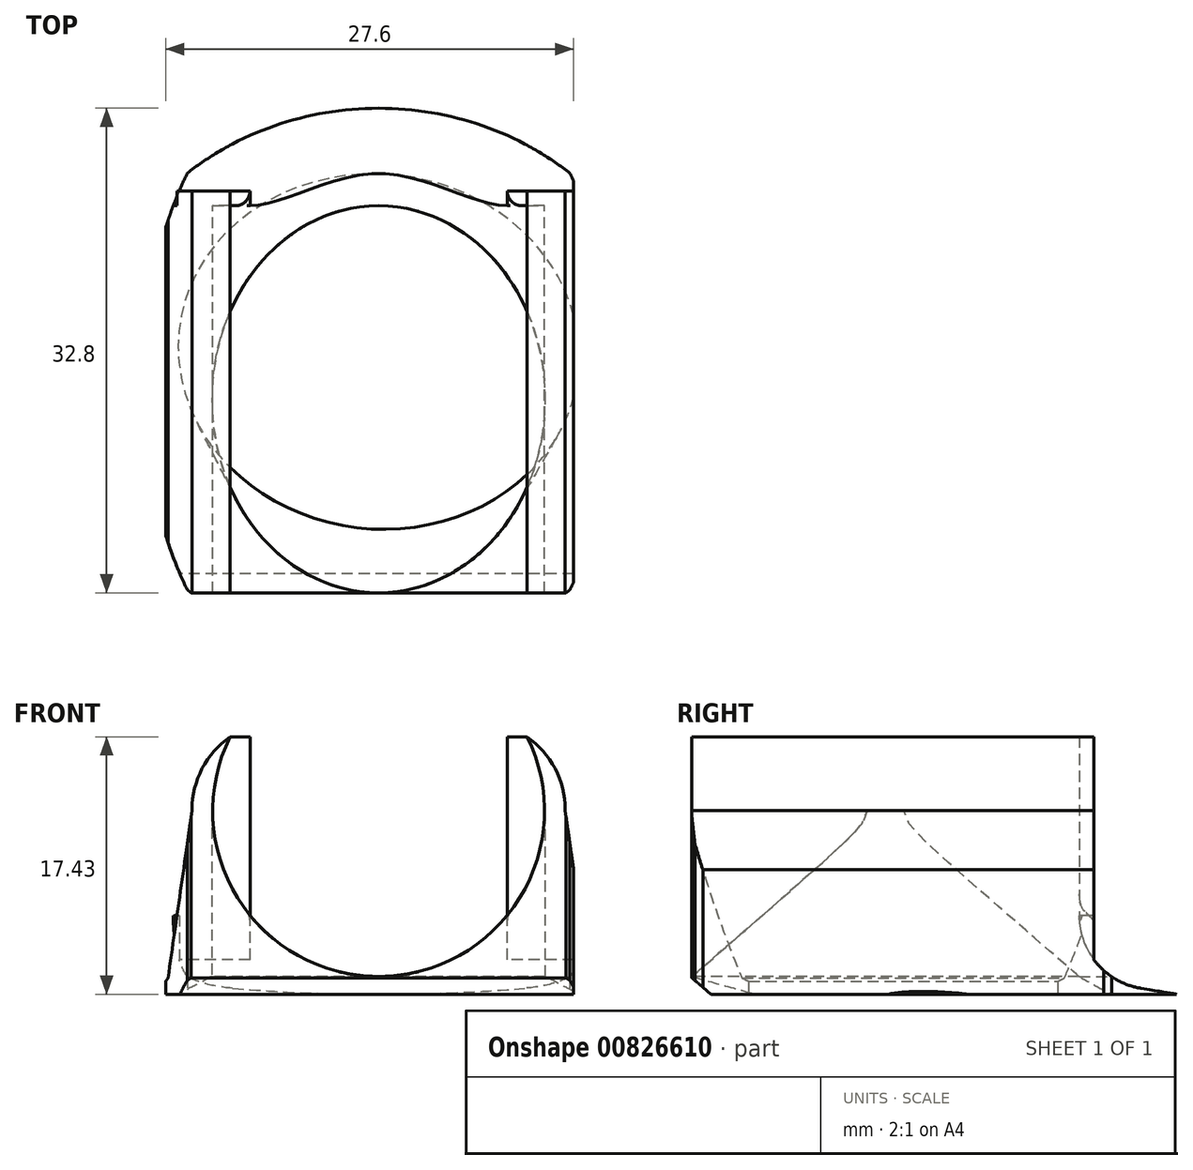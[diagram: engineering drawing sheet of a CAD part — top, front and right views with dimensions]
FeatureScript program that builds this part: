
annotation { "Feature Type Name" : "Feature", "Feature Type Description" : "" }
export const myFeature = defineFeature(function(context is Context, id is Id, definition is map)
    precondition{}
    {
        {
            assignVariable(context, id + "F0", {"name" : "tol", "anyValue" : 0.2});
        }
        {
            var Q0;
            Q0=qCreatedBy(makeId("Top.planeOp"),FACE);
            var sketch = newSketch(context, id + "F1", { "sketchPlane" : qUnion([Q0])});
            skCircle(sketch, "E0", {"center": v(0, 0) * mm, "radius": 13.5 * mm, "construction": true});
            skLineSegment(sketch, "E1.bottom", {"start": v(13.5, 13.5) * mm, "end": v(-13.5, 13.5) * mm, "construction": true});
            skLineSegment(sketch, "E1.top", {"start": v(13.5, -13.5) * mm, "end": v(-13.5, -13.5) * mm, "construction": true});
            skLineSegment(sketch, "E1.left", {"start": v(13.5, 13.5) * mm, "end": v(13.5, -13.5) * mm, "construction": true});
            skLineSegment(sketch, "E1.right", {"start": v(-13.5, 13.5) * mm, "end": v(-13.5, -13.5) * mm, "construction": true});
            skLineSegment(sketch, "E2.0", {"start": v(15, 15) * mm, "end": v(-15, 15) * mm});
            skLineSegment(sketch, "E2.1", {"start": v(15, 15) * mm, "end": v(15, -16.5) * mm});
            skLineSegment(sketch, "E2.3", {"start": v(-15, 15) * mm, "end": v(-15, -16.5) * mm});
            skLineSegment(sketch, "E3", {"start": v(15, -16.5) * mm, "end": v(-15, -16.5) * mm});
            skSolve(sketch);
        }
        {
            var Q0;
            Q0=qCreatedBy(makeId("Top.planeOp"),FACE);
            cPlane(context, id + "F2", {"entities" : qUnion([Q0]), "cplaneType" : CPlaneType.OFFSET, "offset" : 1.1 * mm, "width" : 150 * mm, "height" : 150 * mm});
        }
        {
            var Q0;
            Q0=qCreatedBy(id+"F2.planeOp",FACE);
            var sketch = newSketch(context, id + "F3", { "sketchPlane" : qUnion([Q0])});
            skLineSegment(sketch, "E4.bottom", {"start": v(-14.25, -17.8) * mm, "end": v(14.25, -17.8) * mm});
            skLineSegment(sketch, "E4.top", {"start": v(-14.25, 8.4) * mm, "end": v(14.25, 8.4) * mm});
            skLineSegment(sketch, "E4.left", {"start": v(-14.25, -17.8) * mm, "end": v(-14.25, 8.4) * mm});
            skLineSegment(sketch, "E4.right", {"start": v(14.25, -17.8) * mm, "end": v(14.25, 8.4) * mm});
            skPoint(sketch, "E5", {"position": v(0, -17.8) * mm});
            skSolve(sketch);
        }
        {
            var Q0;
            Q0=makeQuery(id+"F1.imprint","IMPRINT",FACE,{"disambiguationData":[TD([[makeQuery(id+"F1.imprint","IMPRINT",EDGE,{"derivedFrom":sQuery(id+"F1.wireOp",EDGE,"E2.0")}),1.0]])]});
            var Q1;
            Q1=makeQuery(id+"F3.imprint","IMPRINT",FACE,{"disambiguationData":[TD([[makeQuery(id+"F3.imprint","IMPRINT",EDGE,{"derivedFrom":sQuery(id+"F3.wireOp",EDGE,"E4.bottom")}),1.0]])]});
            loft(context, id + "F4", {"sheetProfilesArray" : [{ "sheetProfileEntities" : qUnion([Q0]) }, { "sheetProfileEntities" : qUnion([Q1]) }]});
        }
        {
            var Q0;
            Q0=qCreatedBy(id+"F2.planeOp",FACE);
            cPlane(context, id + "F5", {"entities" : qUnion([Q0]), "cplaneType" : CPlaneType.OFFSET, "offset" : (22.25 / 2 + getVariable(context, 'tol')) * mm, "width" : 150 * mm, "height" : 150 * mm});
        }
        {
            var Q0;
            Q0=qCreatedBy(id+"F5.planeOp",FACE);
            var sketch = newSketch(context, id + "F6", { "sketchPlane" : qUnion([Q0])});
            skLineSegment(sketch, "E6.bottom", {"start": v(-12.62, 8.4) * mm, "end": v(12.62, 8.4) * mm});
            skLineSegment(sketch, "E6.top", {"start": v(-12.63, -17.8) * mm, "end": v(12.63, -17.8) * mm});
            skLineSegment(sketch, "E6.left", {"start": v(-12.62, 8.4) * mm, "end": v(-12.63, -17.8) * mm});
            skLineSegment(sketch, "E6.right", {"start": v(12.63, 8.4) * mm, "end": v(12.62, -17.8) * mm});
            skPoint(sketch, "E7", {"position": v(0, -17.8) * mm});
            skSolve(sketch);
        }
        {
            var Q1;
            Q1=makeQuery(id+"F3.imprint","IMPRINT",FACE,{"disambiguationData":[TD([[makeQuery(id+"F3.imprint","IMPRINT",EDGE,{"derivedFrom":sQuery(id+"F3.wireOp",EDGE,"E4.bottom")}),1.0]])]});
            var Q2;
            Q2=makeQuery(id+"F6.imprint","IMPRINT",FACE,{"disambiguationData":[TD([[makeQuery(id+"F6.imprint","IMPRINT",EDGE,{"derivedFrom":sQuery(id+"F6.wireOp",EDGE,"E6.bottom")}),-1.0]])]});
            loft(context, id + "F7", {"operationType" : NewBodyOperationType.ADD, "sheetProfilesArray" : [{ "sheetProfileEntities" : qUnion([Q1]) }, { "sheetProfileEntities" : qUnion([Q2]) }]});
        }
        {
            var Q0;
            {var subQ0=sQuery(id+"F3.wireOp",EDGE,"E4.right");var subQ1=sQuery(id+"F3.wireOp",EDGE,"E4.left");var subQ2=sQuery(id+"F3.wireOp",EDGE,"E4.top");Q0=makeQuery(id+"F7.boolean.opBoolean","MERGE",EDGE,{"derivedFrom":[makeQuery(id+"F4.opLoft","MID_CAP_EDGE",EDGE,{"disambiguationData":[OSD([subQ2,subQ1,subQ0])],"capPos":1.0}),makeQuery(id+"F7.opLoft","MID_CAP_EDGE",EDGE,{"disambiguationData":[OSD([subQ2,subQ1,subQ0])],"capPos":0.0})]});}
            fillet(context, id + "F8", {"entities" : qUnion([Q0]), "radius" : 5 * mm, "tangentPropagation" : true, "allowEdgeOverflow" : false});
        }
        {
            var Q0;
            Q0=makeQuery(id+"F7.opLoft","CAP_FACE",FACE,{"disambiguationData":[OSD([makeQuery(id+"F6.imprint","IMPRINT",FACE,{"disambiguationData":[TD([[makeQuery(id+"F6.imprint","IMPRINT",EDGE,{"derivedFrom":sQuery(id+"F6.wireOp",EDGE,"E6.bottom")}),-1.0]])]})])],"isStart":true});
            extrude(context, id + "F9", {"entities" : qUnion([Q0]), "operationType" : NewBodyOperationType.ADD, "depth" : 5 * mm, "offsetDistance" : 25 * mm});
        }
        {
            var Q0;
            {var subQ0=sQuery(id+"F6.wireOp",EDGE,"E6.right");var subQ1=sQuery(id+"F6.wireOp",EDGE,"E6.left");var subQ2=sQuery(id+"F6.wireOp",EDGE,"E6.bottom");Q0=makeQuery(id+"F9.boolean.opBoolean","MERGE",FACE,{"derivedFrom":[makeQuery(id+"F7.opLoft","SWEPT_FACE",FACE,{"disambiguationData":[OSD([sQuery(id+"F3.wireOp",EDGE,"E4.top"),sQuery(id+"F3.wireOp",EDGE,"E4.left"),sQuery(id+"F3.wireOp",EDGE,"E4.right"),subQ2,subQ1,subQ0])]}),makeQuery(id+"F9.opExtrude","SWEPT_FACE",FACE,{"disambiguationData":[OSD([subQ2,subQ1,subQ0])]})]});}
            var sketch = newSketch(context, id + "F10", { "sketchPlane" : qUnion([Q0])});
            skLineSegment(sketch, "E8", {"start": v(12.62, 12.43) * mm, "end": v(-12.62, 12.42) * mm, "construction": true});
            skPoint(sketch, "E9", {"position": v(0, 12.42) * mm});
            skCircle(sketch, "E10", {"center": v(0, 12.42) * mm, "radius": 11.23 * mm});
            skPoint(sketch, "E11", {"position": v(0, 1.2) * mm});
            skSolve(sketch);
        }
        {
            var Q0;
            Q0 = qSketchRegion(id + "F10", true);
            extrude(context, id + "F11", {"entities" : qUnion([Q0]), "operationType" : NewBodyOperationType.REMOVE, "endBound" : BoundingType.THROUGH_ALL, "oppositeDirection" : true, "depth" : 25 * mm, "offsetDistance" : 25 * mm, "hasSecondDirection" : true, "secondDirectionBound" : SecondDirectionBoundingType.THROUGH_ALL, "secondDirectionOppositeDirection" : false, "secondDirectionDepth" : 25 * mm});
        }
        {
            var Q0;
            Q0=makeQuery(id+"F9.opExtrude","CAP_EDGE",EDGE,{"disambiguationData":[OSD([sQuery(id+"F6.wireOp",EDGE,"E6.bottom"),sQuery(id+"F6.wireOp",EDGE,"E6.top"),sQuery(id+"F6.wireOp",EDGE,"E6.left")])],"isStart":false});
            var Q1;
            Q1=makeQuery(id+"F9.opExtrude","CAP_EDGE",EDGE,{"disambiguationData":[OSD([sQuery(id+"F6.wireOp",EDGE,"E6.bottom"),sQuery(id+"F6.wireOp",EDGE,"E6.top"),sQuery(id+"F6.wireOp",EDGE,"E6.right")])],"isStart":false});
            fillet(context, id + "F12", {"entities" : qUnion([Q0, Q1]), "radius" : 6 * mm, "tangentPropagation" : true, "allowEdgeOverflow" : false});
        }
        {
            var Q0;
            Q0=sQuery(id+"F10.wireOp",VERTEX,"E8.start");
            var Q1;
            Q1=sQuery(id+"F10.wireOp",VERTEX,"E8.end");
            var Q2;
            {var subQ0=sQuery(id+"F6.wireOp",EDGE,"E6.right");var subQ1=sQuery(id+"F6.wireOp",EDGE,"E6.top");Q2=makeQuery(id+"F9.boolean.opBoolean","MERGE",VERTEX,{"derivedFrom":[makeQuery(id+"F7.opLoft","MID_CAP_VERTEX",VERTEX,{"disambiguationData":[OSD([subQ1,subQ0])],"capPos":1.0}),makeQuery(id+"F9.opExtrude","CAP_VERTEX",VERTEX,{"disambiguationData":[OSD([subQ1,subQ0])],"isStart":true})]});}
            cPlane(context, id + "F13", {"entities" : qUnion([Q0, Q1, Q2]), "cplaneType" : CPlaneType.THREE_POINT, "offset" : 25 * mm, "width" : 150 * mm, "height" : 150 * mm});
        }
        {
            var Q0;
            Q0=qCreatedBy(id+"F13.planeOp",FACE);
            var sketch = newSketch(context, id + "F14", { "sketchPlane" : qUnion([Q0])});
            skLineSegment(sketch, "E12", {"start": v(-11.23, 8.4) * mm, "end": v(-11.23, -17.8) * mm, "construction": true});
            skLineSegment(sketch, "E13", {"start": v(11.22, -17.8) * mm, "end": v(11.22, 8.4) * mm, "construction": true});
            skLineSegment(sketch, "E14.0", {"start": v(-12.62, 8.4) * mm, "end": v(12.62, 8.4) * mm, "construction": true});
            skLineSegment(sketch, "E15.0", {"start": v(-14.25, -17.8) * mm, "end": v(14.25, -17.8) * mm, "construction": true});
            skLineSegment(sketch, "E16", {"start": v(-11.23, 8.4) * mm, "end": v(11.22, -17.8) * mm, "construction": true});
            skPoint(sketch, "E17", {"position": v(0, -4.7) * mm});
            skEllipse(sketch, "E18", {"center": v(0, -4.7) * mm, "majorRadius": 13.1 * mm, "minorRadius": 11.27 * mm, "majorAxis": v(0, 1)});
            skSolve(sketch);
        }
        {
            var Q0;
            Q0 = qSketchRegion(id + "F14", true);
            var Q1;
            Q1=sQuery(id+"F10.wireOp",VERTEX,"E11");
            extrude(context, id + "F15", {"entities" : qUnion([Q0]), "operationType" : NewBodyOperationType.REMOVE, "endBound" : BoundingType.UP_TO_VERTEX, "oppositeDirection" : true, "depth" : 25 * mm, "endBoundEntityVertex" : qUnion([Q1]), "offsetDistance" : 25 * mm});
        }
        {
            var Q0;
            Q0=makeQuery(id+"F1.imprint","IMPRINT",FACE,{"disambiguationData":[TD([[makeQuery(id+"F1.imprint","IMPRINT",EDGE,{"derivedFrom":sQuery(id+"F1.wireOp",EDGE,"E2.0")}),1.0]])]});
            var sketch = newSketch(context, id + "F16", { "sketchPlane" : qUnion([Q0])});
            skCircle(sketch, "E19.0", {"center": v(0, 0) * mm, "radius": 13.5 * mm, "construction": true});
            skEllipse(sketch, "E20", {"center": v(0, -1.48) * mm, "majorRadius": 13.58 * mm, "minorRadius": 12 * mm, "majorAxis": v(1, -0.1)});
            skPoint(sketch, "E21", {"position": v(-13.5, 0) * mm});
            skPoint(sketch, "E22", {"position": v(0, -13.5) * mm});
            skPoint(sketch, "E23", {"position": v(0, 10.55) * mm});
            skSolve(sketch);
        }
        {
            var Q0;
            Q0=makeQuery(id+"F15.boolean.opBoolean","COPY",FACE,{"derivedFrom":makeQuery(id+"F15.opExtrude","CAP_FACE",FACE,{"disambiguationData":[OSD([sQuery(id+"F14.wireOp",EDGE,"E18")])],"isStart":false})});
            var sketch = newSketch(context, id + "F17", { "sketchPlane" : qUnion([Q0])});
            skEllipse(sketch, "E24.0", {"center": v(0, -4.7) * mm, "majorRadius": 13.1 * mm, "minorRadius": 11.27 * mm, "majorAxis": v(0, 1)});
            skSolve(sketch);
        }
        {
            var Q1;
            {var subQ0=sQuery(id+"F17.wireOp",EDGE,"E24.0");var subQ1=makeQuery(id+"F17.imprint","IMPRINT",VERTEX,{"disambiguationData":[OD(0.0)],"derivedFrom":subQ0});Q1=makeQuery(id+"F17.imprint","IMPRINT",FACE,{"disambiguationData":[TD([[makeQuery(id+"F17.imprint","IMPRINT",EDGE,{"disambiguationData":[TD([[subQ1,-1.0]])],"derivedFrom":subQ0}),1.0]])]});}
            var Q2;
            Q2=makeQuery(id+"F16.imprint","IMPRINT",FACE,{"disambiguationData":[TD([[makeQuery(id+"F16.imprint","IMPRINT",EDGE,{"derivedFrom":sQuery(id+"F16.wireOp",EDGE,"E20")}),1.0]])]});
            loft(context, id + "F18", {"operationType" : NewBodyOperationType.REMOVE, "sheetProfilesArray" : [{ "sheetProfileEntities" : qUnion([Q1]) }, { "sheetProfileEntities" : qUnion([Q2]) }]});
        }
        {
            var Q0;
            Q0=qCreatedBy(makeId("Top.planeOp"),FACE);
            var sketch = newSketch(context, id + "F19", { "sketchPlane" : qUnion([Q0])});
            skEllipse(sketch, "E25", {"center": v(0, -3.5) * mm, "majorRadius": 18.5 * mm, "minorRadius": 20 * mm, "majorAxis": v(0, 1)});
            skLineSegment(sketch, "E26.bottom", {"start": v(25, 25) * mm, "end": v(-25, 25) * mm});
            skLineSegment(sketch, "E26.top", {"start": v(25, -25) * mm, "end": v(-25, -25) * mm});
            skLineSegment(sketch, "E26.left", {"start": v(25, 25) * mm, "end": v(25, -25) * mm});
            skLineSegment(sketch, "E26.right", {"start": v(-25, 25) * mm, "end": v(-25, -25) * mm});
            skPoint(sketch, "E26.middle", {"position": v(0, 0) * mm});
            skEllipse(sketch, "E27", {"center": v(0, -3.5) * mm, "majorRadius": 24 * mm, "minorRadius": 16 * mm, "majorAxis": v(0, 1)});
            skSolve(sketch);
        }
        {
            var Q0;
            Q0=makeQuery(id+"F19.imprint","IMPRINT",FACE,{"disambiguationData":[TD([[makeQuery(id+"F19.imprint","IMPRINT",EDGE,{"derivedFrom":sQuery(id+"F19.wireOp",EDGE,"E26.bottom")}),1.0]])]});
            var Q1;
            {var subQ0=sQuery(id+"F19.wireOp",EDGE,"E27");var subQ1=sQuery(id+"F19.wireOp",EDGE,"E25");var subQ2=makeQuery(id+"F19.imprint","INTERSECT",VERTEX,{"disambiguationData":[OD(2.0)],"derivedFrom":[subQ1,subQ0]});Q1=makeQuery(id+"F19.imprint","IMPRINT",FACE,{"disambiguationData":[TD([[makeQuery(id+"F19.imprint","IMPRINT",EDGE,{"disambiguationData":[TD([[subQ2,-1.0]])],"derivedFrom":subQ1}),-1.0]])]});}
            var Q2;
            {var subQ0=sQuery(id+"F19.wireOp",EDGE,"E27");var subQ1=sQuery(id+"F19.wireOp",EDGE,"E25");var subQ2=makeQuery(id+"F19.imprint","INTERSECT",VERTEX,{"disambiguationData":[OD(1.0)],"derivedFrom":[subQ1,subQ0]});Q2=makeQuery(id+"F19.imprint","IMPRINT",FACE,{"disambiguationData":[TD([[makeQuery(id+"F19.imprint","IMPRINT",EDGE,{"disambiguationData":[TD([[subQ2,1.0]])],"derivedFrom":subQ1}),1.0]])]});}
            var Q3;
            {var subQ0=sQuery(id+"F19.wireOp",EDGE,"E27");var subQ1=sQuery(id+"F19.wireOp",EDGE,"E25");var subQ2=makeQuery(id+"F19.imprint","INTERSECT",VERTEX,{"disambiguationData":[OD(0.0)],"derivedFrom":[subQ1,subQ0]});Q3=makeQuery(id+"F19.imprint","IMPRINT",FACE,{"disambiguationData":[TD([[makeQuery(id+"F19.imprint","IMPRINT",EDGE,{"disambiguationData":[TD([[subQ2,1.0]])],"derivedFrom":subQ1}),-1.0]])]});}
            var Q4;
            {var subQ0=sQuery(id+"F19.wireOp",EDGE,"E27");var subQ1=sQuery(id+"F19.wireOp",EDGE,"E25");var subQ2=makeQuery(id+"F19.imprint","INTERSECT",VERTEX,{"disambiguationData":[OD(0.0)],"derivedFrom":[subQ1,subQ0]});Q4=makeQuery(id+"F19.imprint","IMPRINT",FACE,{"disambiguationData":[TD([[makeQuery(id+"F19.imprint","IMPRINT",EDGE,{"disambiguationData":[TD([[subQ2,-1.0]])],"derivedFrom":subQ1}),1.0]])]});}
            extrude(context, id + "F20", {"entities" : qUnion([Q0, Q1, Q2, Q3, Q4]), "operationType" : NewBodyOperationType.REMOVE, "endBound" : BoundingType.THROUGH_ALL, "depth" : 25 * mm, "offsetDistance" : 25 * mm});
        }
        {
            var Q0;
            {var subQ0=sQuery(id+"F6.wireOp",EDGE,"E6.bottom");var subQ1=sQuery(id+"F6.wireOp",EDGE,"E6.top");var subQ2=sQuery(id+"F6.wireOp",EDGE,"E6.left");var subQ3=sQuery(id+"F6.wireOp",EDGE,"E6.right");var subQ4=sQuery(id+"F3.wireOp",EDGE,"E4.right");var subQ5=sQuery(id+"F3.wireOp",EDGE,"E4.left");var subQ6=sQuery(id+"F3.wireOp",EDGE,"E4.top");Q0=makeQuery(id+"F11.boolean.opBoolean","SPLIT",FACE,{"disambiguationData":[TD([makeQuery(id+"F9.opExtrude","SWEPT_FACE",FACE,{"disambiguationData":[OSD([subQ0,subQ1,subQ2])]})])],"derivedFrom":makeQuery(id+"F9.boolean.opBoolean","MERGE",FACE,{"derivedFrom":[makeQuery(id+"F7.opLoft","SWEPT_FACE",FACE,{"disambiguationData":[OSD([subQ6,subQ5,subQ4,subQ0,subQ2,subQ3])]}),makeQuery(id+"F9.opExtrude","SWEPT_FACE",FACE,{"disambiguationData":[OSD([subQ0,subQ2,subQ3])]})]})});}
            var Q1;
            {var subQ0=sQuery(id+"F6.wireOp",EDGE,"E6.bottom");var subQ1=sQuery(id+"F6.wireOp",EDGE,"E6.top");var subQ2=sQuery(id+"F6.wireOp",EDGE,"E6.left");var subQ3=sQuery(id+"F6.wireOp",EDGE,"E6.right");var subQ4=sQuery(id+"F3.wireOp",EDGE,"E4.right");var subQ5=sQuery(id+"F3.wireOp",EDGE,"E4.left");var subQ6=sQuery(id+"F3.wireOp",EDGE,"E4.top");Q1=makeQuery(id+"F11.boolean.opBoolean","SPLIT",FACE,{"disambiguationData":[TD([makeQuery(id+"F9.opExtrude","SWEPT_FACE",FACE,{"disambiguationData":[OSD([subQ0,subQ1,subQ3])]})])],"derivedFrom":makeQuery(id+"F9.boolean.opBoolean","MERGE",FACE,{"derivedFrom":[makeQuery(id+"F7.opLoft","SWEPT_FACE",FACE,{"disambiguationData":[OSD([subQ6,subQ5,subQ4,subQ0,subQ2,subQ3])]}),makeQuery(id+"F9.opExtrude","SWEPT_FACE",FACE,{"disambiguationData":[OSD([subQ0,subQ2,subQ3])]})]})});}
            extrude(context, id + "F21", {"entities" : qUnion([Q0, Q1]), "operationType" : NewBodyOperationType.ADD, "depth" : 1 * mm, "offsetDistance" : 25 * mm});
        }
        {
            var Q0;
            {var subQ0=sQuery(id+"F3.wireOp",EDGE,"E4.right");var subQ1=sQuery(id+"F3.wireOp",EDGE,"E4.left");var subQ2=sQuery(id+"F3.wireOp",EDGE,"E4.top");var subQ3=sQuery(id+"F6.wireOp",EDGE,"E6.right");var subQ4=sQuery(id+"F6.wireOp",EDGE,"E6.left");var subQ5=sQuery(id+"F6.wireOp",EDGE,"E6.bottom");var subQ6=makeQuery(id+"F7.opLoft","SWEPT_FACE",FACE,{"disambiguationData":[OSD([subQ2,subQ1,subQ0,subQ5,subQ4,subQ3])]});Q0=makeQuery(id+"F21.opExtrude","SWEPT_FACE",FACE,{"disambiguationData":[OSD([subQ2,subQ1,subQ0,subQ5,subQ4,subQ3]),TDD([makeQuery(id+"F11.boolean.opBoolean","SPLIT",EDGE,{"disambiguationData":[TD([makeQuery(id+"F7.opLoft","SWEPT_FACE",FACE,{"disambiguationData":[OSD([sQuery(id+"F3.wireOp",EDGE,"E4.bottom"),subQ2,subQ1,subQ5,sQuery(id+"F6.wireOp",EDGE,"E6.top"),subQ4])]})])],"derivedFrom":makeQuery(id+"F8.opFillet","BLEND_EDGE",EDGE,{"blendedFrom":[makeQuery(id+"F7.boolean.opBoolean","MERGE",EDGE,{"derivedFrom":[makeQuery(id+"F4.opLoft","MID_CAP_EDGE",EDGE,{"disambiguationData":[OSD([subQ2,subQ1,subQ0])],"capPos":1.0}),makeQuery(id+"F7.opLoft","MID_CAP_EDGE",EDGE,{"disambiguationData":[OSD([subQ2,subQ1,subQ0])],"capPos":0.0})]}),subQ6],"blendedInto":[subQ6]})})])]});}
            var Q1;
            {var subQ0=sQuery(id+"F6.wireOp",EDGE,"E6.right");var subQ1=sQuery(id+"F6.wireOp",EDGE,"E6.left");var subQ2=sQuery(id+"F6.wireOp",EDGE,"E6.bottom");var subQ3=sQuery(id+"F3.wireOp",EDGE,"E4.right");var subQ4=sQuery(id+"F3.wireOp",EDGE,"E4.left");var subQ5=sQuery(id+"F3.wireOp",EDGE,"E4.top");var subQ6=makeQuery(id+"F7.opLoft","SWEPT_FACE",FACE,{"disambiguationData":[OSD([subQ5,subQ4,subQ3,subQ2,subQ1,subQ0])]});Q1=makeQuery(id+"F21.opExtrude","SWEPT_FACE",FACE,{"disambiguationData":[OSD([subQ5,subQ4,subQ3,subQ2,subQ1,subQ0]),TDD([makeQuery(id+"F11.boolean.opBoolean","SPLIT",EDGE,{"disambiguationData":[TD([makeQuery(id+"F7.opLoft","SWEPT_FACE",FACE,{"disambiguationData":[OSD([sQuery(id+"F3.wireOp",EDGE,"E4.bottom"),subQ5,subQ3,subQ2,sQuery(id+"F6.wireOp",EDGE,"E6.top"),subQ0])]})])],"derivedFrom":makeQuery(id+"F8.opFillet","BLEND_EDGE",EDGE,{"blendedFrom":[makeQuery(id+"F7.boolean.opBoolean","MERGE",EDGE,{"derivedFrom":[makeQuery(id+"F4.opLoft","MID_CAP_EDGE",EDGE,{"disambiguationData":[OSD([subQ5,subQ4,subQ3])],"capPos":1.0}),makeQuery(id+"F7.opLoft","MID_CAP_EDGE",EDGE,{"disambiguationData":[OSD([subQ5,subQ4,subQ3])],"capPos":0.0})]}),subQ6],"blendedInto":[subQ6]})})])]});}
            var Q2;
            Q2=makeQuery(id+"F8.opFillet","BLEND_FACE",FACE,{"disambiguationData":[OSD([sQuery(id+"F3.wireOp",EDGE,"E4.top"),sQuery(id+"F3.wireOp",EDGE,"E4.left"),sQuery(id+"F3.wireOp",EDGE,"E4.right")])]});
            extrude(context, id + "F22", {"entities" : qUnion([Q0, Q1]), "operationType" : NewBodyOperationType.ADD, "endBound" : BoundingType.UP_TO_SURFACE, "depth" : 25 * mm, "endBoundEntityFace" : qUnion([Q2]), "offsetDistance" : 25 * mm});
        }
        {
            var Q0;
            {var subQ0=sQuery(id+"F10.wireOp",EDGE,"E10");var subQ1=sQuery(id+"F6.wireOp",EDGE,"E6.right");var subQ2=sQuery(id+"F6.wireOp",EDGE,"E6.left");var subQ3=sQuery(id+"F6.wireOp",EDGE,"E6.bottom");var subQ4=sQuery(id+"F3.wireOp",EDGE,"E4.right");var subQ5=sQuery(id+"F3.wireOp",EDGE,"E4.left");var subQ6=sQuery(id+"F3.wireOp",EDGE,"E4.top");var subQ7=makeQuery(id+"F21.opExtrude","CAP_VERTEX",VERTEX,{"disambiguationData":[OSD([subQ6,subQ5,subQ4,subQ3,subQ2,subQ1,subQ0]),TDD([makeQuery(id+"F11.boolean.opBoolean","INTERSECT",VERTEX,{"disambiguationData":[OD(0.0)],"derivedFrom":[makeQuery(id+"F8.opFillet","BLEND_FACE",FACE,{"disambiguationData":[OSD([subQ6,subQ5,subQ4])]}),makeQuery(id+"F9.boolean.opBoolean","MERGE",FACE,{"derivedFrom":[makeQuery(id+"F7.opLoft","SWEPT_FACE",FACE,{"disambiguationData":[OSD([subQ6,subQ5,subQ4,subQ3,subQ2,subQ1])]}),makeQuery(id+"F9.opExtrude","SWEPT_FACE",FACE,{"disambiguationData":[OSD([subQ3,subQ2,subQ1])]})]}),makeQuery(id+"F11.opExtrude","SWEPT_FACE",FACE,{"disambiguationData":[OSD([subQ0])]})]})])],"isStart":false});Q0=makeQuery(id+"F22.boolean.opBoolean","MERGE",VERTEX,{"derivedFrom":[subQ7,makeQuery(id+"F22.opExtrude","CAP_VERTEX",VERTEX,{"disambiguationData":[OSD([subQ6,subQ5,subQ4,subQ3,subQ2,subQ1,subQ0]),TDD([subQ7])],"isStart":true})]});}
            var Q1;
            {var subQ0=sQuery(id+"F10.wireOp",EDGE,"E10");var subQ1=sQuery(id+"F6.wireOp",EDGE,"E6.right");var subQ2=sQuery(id+"F6.wireOp",EDGE,"E6.left");var subQ3=sQuery(id+"F6.wireOp",EDGE,"E6.bottom");var subQ4=sQuery(id+"F3.wireOp",EDGE,"E4.right");var subQ5=sQuery(id+"F3.wireOp",EDGE,"E4.left");var subQ6=sQuery(id+"F3.wireOp",EDGE,"E4.top");var subQ7=makeQuery(id+"F11.boolean.opBoolean","INTERSECT",VERTEX,{"disambiguationData":[OD(0.0)],"derivedFrom":[makeQuery(id+"F8.opFillet","BLEND_FACE",FACE,{"disambiguationData":[OSD([subQ6,subQ5,subQ4])]}),makeQuery(id+"F9.boolean.opBoolean","MERGE",FACE,{"derivedFrom":[makeQuery(id+"F7.opLoft","SWEPT_FACE",FACE,{"disambiguationData":[OSD([subQ6,subQ5,subQ4,subQ3,subQ2,subQ1])]}),makeQuery(id+"F9.opExtrude","SWEPT_FACE",FACE,{"disambiguationData":[OSD([subQ3,subQ2,subQ1])]})]}),makeQuery(id+"F11.opExtrude","SWEPT_FACE",FACE,{"disambiguationData":[OSD([subQ0])]})]});Q1=makeQuery(id+"F22.boolean.opBoolean","MERGE",VERTEX,{"derivedFrom":[makeQuery(id+"F21.boolean.opBoolean","MERGE",VERTEX,{"derivedFrom":[subQ7,makeQuery(id+"F21.opExtrude","CAP_VERTEX",VERTEX,{"disambiguationData":[OSD([subQ6,subQ5,subQ4,subQ3,subQ2,subQ1,subQ0]),TDD([subQ7])],"isStart":true})]}),makeQuery(id+"F22.opExtrude","CAP_VERTEX",VERTEX,{"disambiguationData":[OSD([subQ6,subQ5,subQ4,subQ3,subQ2,subQ1,subQ0]),TDD([makeQuery(id+"F21.opExtrude","SWEPT_EDGE",EDGE,{"disambiguationData":[OSD([subQ6,subQ5,subQ4,subQ3,subQ2,subQ1,subQ0]),TDD([subQ7])]})])],"isStart":false})]});}
            var Q2;
            {var subQ0=sQuery(id+"F10.wireOp",EDGE,"E10");var subQ1=sQuery(id+"F6.wireOp",EDGE,"E6.right");var subQ2=sQuery(id+"F6.wireOp",EDGE,"E6.left");var subQ3=sQuery(id+"F6.wireOp",EDGE,"E6.bottom");var subQ4=sQuery(id+"F3.wireOp",EDGE,"E4.right");var subQ5=sQuery(id+"F3.wireOp",EDGE,"E4.left");var subQ6=sQuery(id+"F3.wireOp",EDGE,"E4.top");var subQ7=makeQuery(id+"F11.boolean.opBoolean","INTERSECT",VERTEX,{"disambiguationData":[OD(1.0)],"derivedFrom":[makeQuery(id+"F8.opFillet","BLEND_FACE",FACE,{"disambiguationData":[OSD([subQ6,subQ5,subQ4])]}),makeQuery(id+"F9.boolean.opBoolean","MERGE",FACE,{"derivedFrom":[makeQuery(id+"F7.opLoft","SWEPT_FACE",FACE,{"disambiguationData":[OSD([subQ6,subQ5,subQ4,subQ3,subQ2,subQ1])]}),makeQuery(id+"F9.opExtrude","SWEPT_FACE",FACE,{"disambiguationData":[OSD([subQ3,subQ2,subQ1])]})]}),makeQuery(id+"F11.opExtrude","SWEPT_FACE",FACE,{"disambiguationData":[OSD([subQ0])]})]});Q2=makeQuery(id+"F22.boolean.opBoolean","MERGE",VERTEX,{"derivedFrom":[makeQuery(id+"F21.boolean.opBoolean","MERGE",VERTEX,{"derivedFrom":[subQ7,makeQuery(id+"F21.opExtrude","CAP_VERTEX",VERTEX,{"disambiguationData":[OSD([subQ6,subQ5,subQ4,subQ3,subQ2,subQ1,subQ0]),TDD([subQ7])],"isStart":true})]}),makeQuery(id+"F22.opExtrude","CAP_VERTEX",VERTEX,{"disambiguationData":[OSD([subQ6,subQ5,subQ4,subQ3,subQ2,subQ1,subQ0]),TDD([makeQuery(id+"F21.opExtrude","SWEPT_EDGE",EDGE,{"disambiguationData":[OSD([subQ6,subQ5,subQ4,subQ3,subQ2,subQ1,subQ0]),TDD([subQ7])]})])],"isStart":false})]});}
            cPlane(context, id + "F23", {"entities" : qUnion([Q0, Q1, Q2]), "cplaneType" : CPlaneType.THREE_POINT, "offset" : 25 * mm, "width" : 150 * mm, "height" : 150 * mm});
        }
        {
            var Q0;
            Q0=qCreatedBy(id+"F23.planeOp",FACE);
            var sketch = newSketch(context, id + "F24", { "sketchPlane" : qUnion([Q0])});
            skLineSegment(sketch, "E28.bottom", {"start": v(-8.7, -9.4) * mm, "end": v(-11.23, -9.4) * mm});
            skLineSegment(sketch, "E28.top", {"start": v(-8.7, -8.4) * mm, "end": v(-11.23, -8.4) * mm});
            skLineSegment(sketch, "E28.left", {"start": v(-8.7, -9.4) * mm, "end": v(-8.7, -8.4) * mm});
            skLineSegment(sketch, "E28.right", {"start": v(-11.23, -9.4) * mm, "end": v(-11.23, -8.4) * mm});
            skLineSegment(sketch, "E29", {"start": v(-11.23, -9.4) * mm, "end": v(-11.23, 17.8) * mm});
            skLineSegment(sketch, "E30", {"start": v(11.22, 17.8) * mm, "end": v(11.22, -9.4) * mm});
            skLineSegment(sketch, "E31", {"start": v(0, 0) * mm, "end": v(0, -10.2) * mm, "construction": true});
            skLineSegment(sketch, "E32.MirrorCS", {"start": v(8.7, -9.4) * mm, "end": v(8.7, -8.4) * mm});
            skLineSegment(sketch, "E33.MirrorCS", {"start": v(8.7, -9.4) * mm, "end": v(11.23, -9.4) * mm});
            skLineSegment(sketch, "E34.MirrorCS", {"start": v(11.23, -9.4) * mm, "end": v(11.23, -8.4) * mm});
            skLineSegment(sketch, "E35.MirrorCS", {"start": v(8.7, -8.4) * mm, "end": v(11.23, -8.4) * mm});
            skSolve(sketch);
        }
        {
            var Q0;
            {var subQ0=sQuery(id+"F24.wireOp",EDGE,"E28.bottom");Q0=makeQuery(id+"F24.imprint","IMPRINT",FACE,{"disambiguationData":[TD([[makeQuery(id+"F24.imprint","IMPRINT",EDGE,{"derivedFrom":subQ0}),-1.0]])]});}
            var Q1;
            Q1=makeQuery(id+"F24.imprint","IMPRINT",FACE,{"disambiguationData":[TD([[makeQuery(id+"F24.imprint","IMPRINT",EDGE,{"derivedFrom":sQuery(id+"F24.wireOp",EDGE,"E32.MirrorCS")}),-1.0]])]});
            var Q2;
            {var subQ0=sQuery(id+"F10.wireOp",EDGE,"E10");var subQ1=makeQuery(id+"F11.opExtrude","SWEPT_FACE",FACE,{"disambiguationData":[OSD([subQ0])]});var subQ2=sQuery(id+"F6.wireOp",EDGE,"E6.right");var subQ3=sQuery(id+"F6.wireOp",EDGE,"E6.left");var subQ4=sQuery(id+"F6.wireOp",EDGE,"E6.bottom");var subQ5=sQuery(id+"F3.wireOp",EDGE,"E4.right");var subQ6=sQuery(id+"F3.wireOp",EDGE,"E4.left");var subQ7=sQuery(id+"F3.wireOp",EDGE,"E4.top");var subQ8=makeQuery(id+"F9.boolean.opBoolean","MERGE",FACE,{"derivedFrom":[makeQuery(id+"F7.opLoft","SWEPT_FACE",FACE,{"disambiguationData":[OSD([subQ7,subQ6,subQ5,subQ4,subQ3,subQ2])]}),makeQuery(id+"F9.opExtrude","SWEPT_FACE",FACE,{"disambiguationData":[OSD([subQ4,subQ3,subQ2])]})]});Q2=makeQuery(id+"F21.boolean.opBoolean","MERGE",FACE,{"derivedFrom":[makeQuery(id+"F11.boolean.opBoolean","COPY",FACE,{"derivedFrom":subQ1}),makeQuery(id+"F21.opExtrude","SWEPT_FACE",FACE,{"disambiguationData":[OSD([subQ7,subQ6,subQ5,subQ4,subQ3,subQ2,subQ0]),TDD([makeQuery(id+"F11.boolean.opBoolean","INTERSECT",EDGE,{"disambiguationData":[OD(0.0)],"derivedFrom":[subQ8,subQ1]})])]}),makeQuery(id+"F21.opExtrude","SWEPT_FACE",FACE,{"disambiguationData":[OSD([subQ7,subQ6,subQ5,subQ4,subQ3,subQ2,subQ0]),TDD([makeQuery(id+"F11.boolean.opBoolean","INTERSECT",EDGE,{"disambiguationData":[OD(1.0)],"derivedFrom":[subQ8,subQ1]})])]})]});}
            var Q3;
            {var subQ0=sQuery(id+"F6.wireOp",EDGE,"E6.bottom");var subQ1=sQuery(id+"F6.wireOp",EDGE,"E6.top");var subQ2=sQuery(id+"F6.wireOp",EDGE,"E6.left");var subQ3=sQuery(id+"F6.wireOp",EDGE,"E6.right");var subQ4=sQuery(id+"F10.wireOp",EDGE,"E10");var subQ5=makeQuery(id+"F11.opExtrude","SWEPT_FACE",FACE,{"disambiguationData":[OSD([subQ4])]});var subQ6=sQuery(id+"F3.wireOp",EDGE,"E4.right");var subQ7=sQuery(id+"F3.wireOp",EDGE,"E4.left");var subQ8=sQuery(id+"F3.wireOp",EDGE,"E4.top");Q3=makeQuery(id+"F21.opExtrude","CAP_VERTEX",VERTEX,{"disambiguationData":[OSD([subQ8,subQ7,subQ6,subQ0,subQ1,subQ2,subQ3,subQ4]),TDD([makeQuery(id+"F12.opFillet","BLEND_VERTEX",VERTEX,{"blendedFrom":[makeQuery(id+"F9.opExtrude","CAP_EDGE",EDGE,{"disambiguationData":[OSD([subQ0,subQ1,subQ2])],"isStart":false}),makeQuery(id+"F11.boolean.opBoolean","COPY",FACE,{"derivedFrom":subQ5}),makeQuery(id+"F11.boolean.opBoolean","SPLIT",FACE,{"disambiguationData":[TD([makeQuery(id+"F9.opExtrude","SWEPT_FACE",FACE,{"disambiguationData":[OSD([subQ0,subQ1,subQ2])]})])],"derivedFrom":makeQuery(id+"F9.boolean.opBoolean","MERGE",FACE,{"derivedFrom":[makeQuery(id+"F7.opLoft","SWEPT_FACE",FACE,{"disambiguationData":[OSD([subQ8,subQ7,subQ6,subQ0,subQ2,subQ3])]}),makeQuery(id+"F9.opExtrude","SWEPT_FACE",FACE,{"disambiguationData":[OSD([subQ0,subQ2,subQ3])]})]})})],"blendedInto":[makeQuery(id+"F11.boolean.opBoolean","COPY",FACE,{"derivedFrom":subQ5}),makeQuery(id+"F11.boolean.opBoolean","SPLIT",FACE,{"disambiguationData":[TD([makeQuery(id+"F9.opExtrude","SWEPT_FACE",FACE,{"disambiguationData":[OSD([subQ0,subQ1,subQ2])]})])],"derivedFrom":makeQuery(id+"F9.boolean.opBoolean","MERGE",FACE,{"derivedFrom":[makeQuery(id+"F7.opLoft","SWEPT_FACE",FACE,{"disambiguationData":[OSD([subQ8,subQ7,subQ6,subQ0,subQ2,subQ3])]}),makeQuery(id+"F9.opExtrude","SWEPT_FACE",FACE,{"disambiguationData":[OSD([subQ0,subQ2,subQ3])]})]})})]})])],"isStart":false});}
            extrude(context, id + "F25", {"entities" : qUnion([Q0, Q1]), "operationType" : NewBodyOperationType.ADD, "endBound" : BoundingType.UP_TO_VERTEX, "oppositeDirection" : true, "depth" : 25 * mm, "endBoundEntityFace" : qUnion([Q2]), "endBoundEntityVertex" : qUnion([Q3]), "offsetDistance" : 25 * mm});
        }
        {
            var Q0;
            {var subQ0=sQuery(id+"F3.wireOp",EDGE,"E4.right");var subQ1=sQuery(id+"F3.wireOp",EDGE,"E4.left");var subQ2=sQuery(id+"F3.wireOp",EDGE,"E4.top");var subQ4=sQuery(id+"F6.wireOp",EDGE,"E6.right");var subQ5=sQuery(id+"F6.wireOp",EDGE,"E6.left");var subQ6=sQuery(id+"F6.wireOp",EDGE,"E6.bottom");var subQ7=makeQuery(id+"F9.opExtrude","SWEPT_FACE",FACE,{"disambiguationData":[OSD([subQ6,subQ5,subQ4])]});var subQ8=sQuery(id+"F6.wireOp",EDGE,"E6.top");var subQ9=makeQuery(id+"F7.opLoft","SWEPT_FACE",FACE,{"disambiguationData":[OSD([sQuery(id+"F3.wireOp",EDGE,"E4.bottom"),subQ2,subQ1,subQ6,subQ8,subQ5])]});var subQ10=makeQuery(id+"F7.opLoft","SWEPT_FACE",FACE,{"disambiguationData":[OSD([subQ2,subQ1,subQ0,subQ6,subQ5,subQ4])]});Q0=makeQuery(id+"F25.boolean.opBoolean","MERGE",FACE,{"derivedFrom":[makeQuery(id+"F22.boolean.opBoolean","MERGE",FACE,{"derivedFrom":[makeQuery(id+"F21.opExtrude","CAP_FACE",FACE,{"disambiguationData":[OSD([subQ2,subQ1,subQ0,subQ6,subQ5,subQ4]),TDD([makeQuery(id+"F11.boolean.opBoolean","SPLIT",FACE,{"disambiguationData":[TD([makeQuery(id+"F9.opExtrude","SWEPT_FACE",FACE,{"disambiguationData":[OSD([subQ6,subQ8,subQ5])]})])],"derivedFrom":makeQuery(id+"F9.boolean.opBoolean","MERGE",FACE,{"derivedFrom":[subQ10,subQ7]})})])],"isStart":false}),makeQuery(id+"F22.opExtrude","SWEPT_FACE",FACE,{"disambiguationData":[OSD([subQ2,subQ1,subQ0,subQ6,subQ5,subQ4]),TDD([makeQuery(id+"F21.opExtrude","CAP_EDGE",EDGE,{"disambiguationData":[OSD([subQ2,subQ1,subQ0,subQ6,subQ5,subQ4]),TDD([makeQuery(id+"F11.boolean.opBoolean","SPLIT",EDGE,{"disambiguationData":[TD([subQ9])],"derivedFrom":makeQuery(id+"F8.opFillet","BLEND_EDGE",EDGE,{"blendedFrom":[makeQuery(id+"F7.boolean.opBoolean","MERGE",EDGE,{"derivedFrom":[makeQuery(id+"F4.opLoft","MID_CAP_EDGE",EDGE,{"disambiguationData":[OSD([subQ2,subQ1,subQ0])],"capPos":1.0}),makeQuery(id+"F7.opLoft","MID_CAP_EDGE",EDGE,{"disambiguationData":[OSD([subQ2,subQ1,subQ0])],"capPos":0.0})]}),subQ10],"blendedInto":[subQ10]})})])],"isStart":false})])]})]}),makeQuery(id+"F25.opExtrude","SWEPT_FACE",FACE,{"disambiguationData":[OSD([sQuery(id+"F24.wireOp",EDGE,"E28.bottom")])]})]});}
            var sketch = newSketch(context, id + "F26", { "sketchPlane" : qUnion([Q0])});
            skArc(sketch, "E36.0", {"start": v(11.23, 16.35) * mm, "mid": v(10.67, 16.93) * mm, "end": v(10.05, 17.42) * mm});
            skArc(sketch, "E37.0", {"start": v(-11.22, 16.35) * mm, "mid": v(-10.67, 16.93) * mm, "end": v(-10.05, 17.43) * mm});
            skLineSegment(sketch, "E38.0", {"start": v(-11.23, 17.42) * mm, "end": v(-11.23, 16.35) * mm});
            skLineSegment(sketch, "E39.0", {"start": v(-8.7, 17.42) * mm, "end": v(-11.23, 17.42) * mm});
            skLineSegment(sketch, "E40.0", {"start": v(11.23, 17.42) * mm, "end": v(11.23, 16.35) * mm});
            skLineSegment(sketch, "E41.0", {"start": v(8.7, 17.42) * mm, "end": v(11.23, 17.42) * mm});
            skSolve(sketch);
        }
        {
            var Q0;
            Q0 = qSketchRegion(id + "F26", true);
            extrude(context, id + "F27", {"entities" : qUnion([Q0]), "operationType" : NewBodyOperationType.REMOVE, "endBound" : BoundingType.THROUGH_ALL, "oppositeDirection" : true, "depth" : 25 * mm, "offsetDistance" : 25 * mm});
        }
        {
            var Q0;
            Q0=makeQuery(id+"F25.opExtrude","SWEPT_EDGE",EDGE,{"disambiguationData":[OSD([sQuery(id+"F24.wireOp",EDGE,"E28.top"),sQuery(id+"F24.wireOp",EDGE,"E28.left")])]});
            var Q1;
            Q1=makeQuery(id+"F25.opExtrude","SWEPT_EDGE",EDGE,{"disambiguationData":[OSD([sQuery(id+"F24.wireOp",EDGE,"E32.MirrorCS"),sQuery(id+"F24.wireOp",EDGE,"E35.MirrorCS")])]});
            fillet(context, id + "F28", {"entities" : qUnion([Q0, Q1]), "radius" : 1 * mm, "tangentPropagation" : true, "allowEdgeOverflow" : false});
        }
        {
            var Q0;
            {var subQ0=sQuery(id+"F6.wireOp",EDGE,"E6.right");var subQ1=sQuery(id+"F6.wireOp",EDGE,"E6.left");var subQ2=sQuery(id+"F6.wireOp",EDGE,"E6.bottom");var subQ3=sQuery(id+"F3.wireOp",EDGE,"E4.right");var subQ4=sQuery(id+"F3.wireOp",EDGE,"E4.left");var subQ5=sQuery(id+"F3.wireOp",EDGE,"E4.top");var subQ6=sQuery(id+"F6.wireOp",EDGE,"E6.top");var subQ7=sQuery(id+"F3.wireOp",EDGE,"E4.bottom");Q0=makeQuery(id+"F22.opExtrude","SWEPT_FACE",FACE,{"disambiguationData":[OSD([subQ7,subQ5,subQ4,subQ3,subQ2,subQ6,subQ1,subQ0]),TDD([makeQuery(id+"F21.opExtrude","SWEPT_EDGE",EDGE,{"disambiguationData":[OSD([subQ7,subQ5,subQ4,subQ3,subQ2,subQ6,subQ1,subQ0]),TDD([makeQuery(id+"F8.opFillet","BLEND_VERTEX",VERTEX,{"blendedFrom":[makeQuery(id+"F7.boolean.opBoolean","MERGE",EDGE,{"derivedFrom":[makeQuery(id+"F4.opLoft","MID_CAP_EDGE",EDGE,{"disambiguationData":[OSD([subQ5,subQ4,subQ3])],"capPos":1.0}),makeQuery(id+"F7.opLoft","MID_CAP_EDGE",EDGE,{"disambiguationData":[OSD([subQ5,subQ4,subQ3])],"capPos":0.0})]}),makeQuery(id+"F7.opLoft","SWEPT_FACE",FACE,{"disambiguationData":[OSD([subQ7,subQ5,subQ4,subQ2,subQ6,subQ1])]}),makeQuery(id+"F7.opLoft","SWEPT_FACE",FACE,{"disambiguationData":[OSD([subQ5,subQ4,subQ3,subQ2,subQ1,subQ0])]})],"blendedInto":[makeQuery(id+"F7.opLoft","SWEPT_FACE",FACE,{"disambiguationData":[OSD([subQ7,subQ5,subQ4,subQ2,subQ6,subQ1])]}),makeQuery(id+"F7.opLoft","SWEPT_FACE",FACE,{"disambiguationData":[OSD([subQ5,subQ4,subQ3,subQ2,subQ1,subQ0])]})]})])]})])]});}
            extrude(context, id + "F29", {"entities" : qUnion([Q0]), "operationType" : NewBodyOperationType.REMOVE, "oppositeDirection" : true, "depth" : .5 * mm, "offsetDistance" : 25 * mm});
        }
        {
            var Q0;
            Q0=makeQuery(id+"F29.boolean.opBoolean","COPY",FACE,{"derivedFrom":makeQuery(id+"F29.opExtrude","CAP_FACE",FACE,{"disambiguationData":[OSD([sQuery(id+"F3.wireOp",EDGE,"E4.bottom"),sQuery(id+"F3.wireOp",EDGE,"E4.top"),sQuery(id+"F3.wireOp",EDGE,"E4.left"),sQuery(id+"F3.wireOp",EDGE,"E4.right"),sQuery(id+"F6.wireOp",EDGE,"E6.bottom"),sQuery(id+"F6.wireOp",EDGE,"E6.top"),sQuery(id+"F6.wireOp",EDGE,"E6.left"),sQuery(id+"F6.wireOp",EDGE,"E6.right")])],"isStart":false})});
            var Q1;
            {var subQ6=sQuery(id+"F19.wireOp",EDGE,"E27");var subQ7=sQuery(id+"F19.wireOp",EDGE,"E25");Q1=makeQuery(id+"F20.boolean.opBoolean","COPY",FACE,{"disambiguationData":[TD([makeQuery(id+"F20.opExtrude","SWEPT_FACE",FACE,{"disambiguationData":[OSD([subQ7]),TDD([makeQuery(id+"F19.imprint","IMPRINT",EDGE,{"disambiguationData":[TD([[makeQuery(id+"F19.imprint","INTERSECT",VERTEX,{"disambiguationData":[OD(2.0)],"derivedFrom":[subQ7,subQ6]}),-1.0]])],"derivedFrom":subQ7})])]})])],"derivedFrom":makeQuery(id+"F20.opExtrude","SWEPT_FACE",FACE,{"disambiguationData":[OSD([subQ6]),TDD([makeQuery(id+"F19.imprint","IMPRINT",EDGE,{"disambiguationData":[TD([[makeQuery(id+"F19.imprint","INTERSECT",VERTEX,{"disambiguationData":[OD(1.0)],"derivedFrom":[subQ7,subQ6]}),1.0]])],"derivedFrom":subQ6})])]})});}
            extrude(context, id + "F30", {"entities" : qUnion([Q0]), "operationType" : NewBodyOperationType.ADD, "endBound" : BoundingType.UP_TO_SURFACE, "depth" : 25 * mm, "endBoundEntityFace" : qUnion([Q1]), "offsetDistance" : 25 * mm});
        }
        {
            var Q0;
            {var subQ0=sQuery(id+"F10.wireOp",EDGE,"E10");var subQ1=sQuery(id+"F6.wireOp",EDGE,"E6.right");var subQ2=sQuery(id+"F6.wireOp",EDGE,"E6.left");var subQ3=sQuery(id+"F6.wireOp",EDGE,"E6.bottom");var subQ4=sQuery(id+"F3.wireOp",EDGE,"E4.right");var subQ5=sQuery(id+"F3.wireOp",EDGE,"E4.left");var subQ6=sQuery(id+"F3.wireOp",EDGE,"E4.top");var subQ7=makeQuery(id+"F11.boolean.opBoolean","INTERSECT",VERTEX,{"disambiguationData":[OD(0.0)],"derivedFrom":[makeQuery(id+"F8.opFillet","BLEND_FACE",FACE,{"disambiguationData":[OSD([subQ6,subQ5,subQ4])]}),makeQuery(id+"F9.boolean.opBoolean","MERGE",FACE,{"derivedFrom":[makeQuery(id+"F7.opLoft","SWEPT_FACE",FACE,{"disambiguationData":[OSD([subQ6,subQ5,subQ4,subQ3,subQ2,subQ1])]}),makeQuery(id+"F9.opExtrude","SWEPT_FACE",FACE,{"disambiguationData":[OSD([subQ3,subQ2,subQ1])]})]}),makeQuery(id+"F11.opExtrude","SWEPT_FACE",FACE,{"disambiguationData":[OSD([subQ0])]})]});Q0=makeQuery(id+"F28.opFillet","TWEAK_EDGE",EDGE,{"derivedFrom":[makeQuery(id+"F25.boolean.opBoolean","MERGE",VERTEX,{"derivedFrom":[makeQuery(id+"F22.boolean.opBoolean","MERGE",VERTEX,{"derivedFrom":[makeQuery(id+"F21.boolean.opBoolean","MERGE",VERTEX,{"derivedFrom":[subQ7,makeQuery(id+"F21.opExtrude","CAP_VERTEX",VERTEX,{"disambiguationData":[OSD([subQ6,subQ5,subQ4,subQ3,subQ2,subQ1,subQ0]),TDD([subQ7])],"isStart":true})]}),makeQuery(id+"F22.opExtrude","CAP_VERTEX",VERTEX,{"disambiguationData":[OSD([subQ6,subQ5,subQ4,subQ3,subQ2,subQ1,subQ0]),TDD([makeQuery(id+"F21.opExtrude","SWEPT_EDGE",EDGE,{"disambiguationData":[OSD([subQ6,subQ5,subQ4,subQ3,subQ2,subQ1,subQ0]),TDD([subQ7])]})])],"isStart":false})]}),makeQuery(id+"F25.opExtrude","CAP_VERTEX",VERTEX,{"disambiguationData":[OSD([sQuery(id+"F24.wireOp",EDGE,"E28.top"),sQuery(id+"F24.wireOp",EDGE,"E28.left")])],"isStart":true})]})]});}
            var Q1;
            {var subQ0=sQuery(id+"F10.wireOp",EDGE,"E10");var subQ1=sQuery(id+"F6.wireOp",EDGE,"E6.right");var subQ2=sQuery(id+"F6.wireOp",EDGE,"E6.left");var subQ3=sQuery(id+"F6.wireOp",EDGE,"E6.bottom");var subQ4=sQuery(id+"F3.wireOp",EDGE,"E4.right");var subQ5=sQuery(id+"F3.wireOp",EDGE,"E4.left");var subQ6=sQuery(id+"F3.wireOp",EDGE,"E4.top");var subQ7=makeQuery(id+"F11.boolean.opBoolean","INTERSECT",VERTEX,{"disambiguationData":[OD(1.0)],"derivedFrom":[makeQuery(id+"F8.opFillet","BLEND_FACE",FACE,{"disambiguationData":[OSD([subQ6,subQ5,subQ4])]}),makeQuery(id+"F9.boolean.opBoolean","MERGE",FACE,{"derivedFrom":[makeQuery(id+"F7.opLoft","SWEPT_FACE",FACE,{"disambiguationData":[OSD([subQ6,subQ5,subQ4,subQ3,subQ2,subQ1])]}),makeQuery(id+"F9.opExtrude","SWEPT_FACE",FACE,{"disambiguationData":[OSD([subQ3,subQ2,subQ1])]})]}),makeQuery(id+"F11.opExtrude","SWEPT_FACE",FACE,{"disambiguationData":[OSD([subQ0])]})]});Q1=makeQuery(id+"F28.opFillet","TWEAK_EDGE",EDGE,{"derivedFrom":[makeQuery(id+"F25.boolean.opBoolean","MERGE",VERTEX,{"derivedFrom":[makeQuery(id+"F22.boolean.opBoolean","MERGE",VERTEX,{"derivedFrom":[makeQuery(id+"F21.boolean.opBoolean","MERGE",VERTEX,{"derivedFrom":[subQ7,makeQuery(id+"F21.opExtrude","CAP_VERTEX",VERTEX,{"disambiguationData":[OSD([subQ6,subQ5,subQ4,subQ3,subQ2,subQ1,subQ0]),TDD([subQ7])],"isStart":true})]}),makeQuery(id+"F22.opExtrude","CAP_VERTEX",VERTEX,{"disambiguationData":[OSD([subQ6,subQ5,subQ4,subQ3,subQ2,subQ1,subQ0]),TDD([makeQuery(id+"F21.opExtrude","SWEPT_EDGE",EDGE,{"disambiguationData":[OSD([subQ6,subQ5,subQ4,subQ3,subQ2,subQ1,subQ0]),TDD([subQ7])]})])],"isStart":false})]}),makeQuery(id+"F25.opExtrude","CAP_VERTEX",VERTEX,{"disambiguationData":[OSD([sQuery(id+"F24.wireOp",EDGE,"E32.MirrorCS"),sQuery(id+"F24.wireOp",EDGE,"E35.MirrorCS")])],"isStart":true})]})]});}
            fillet(context, id + "F31", {"entities" : qUnion([Q0, Q1]), "radius" : 1 * mm, "tangentPropagation" : true, "allowEdgeOverflow" : false});
        }
        {
            var Q0;
            Q0=qCreatedBy(makeId("Top.planeOp"),FACE);
            var sketch = newSketch(context, id + "F32", { "sketchPlane" : qUnion([Q0])});
            skLineSegment(sketch, "E42.bottom", {"start": v(-14.4, 18.5) * mm, "end": v(13.2, 18.5) * mm});
            skLineSegment(sketch, "E42.top", {"start": v(-14.4, -18.5) * mm, "end": v(13.2, -18.5) * mm});
            skLineSegment(sketch, "E42.left", {"start": v(-14.4, 18.5) * mm, "end": v(-14.4, -18.5) * mm});
            skLineSegment(sketch, "E42.right", {"start": v(13.2, 18.5) * mm, "end": v(13.2, -18.5) * mm});
            skPoint(sketch, "E43", {"position": v(-0.6, -18.5) * mm});
            skPoint(sketch, "E44", {"position": v(-14.4, 0) * mm});
            skLineSegment(sketch, "E45.0", {"start": v(-19.4, 23.5) * mm, "end": v(-19.4, -23.5) * mm});
            skLineSegment(sketch, "E45.1", {"start": v(-19.4, 23.5) * mm, "end": v(18.2, 23.5) * mm});
            skLineSegment(sketch, "E45.2", {"start": v(18.2, 23.5) * mm, "end": v(18.2, -23.5) * mm});
            skLineSegment(sketch, "E45.3", {"start": v(-19.4, -23.5) * mm, "end": v(18.2, -23.5) * mm});
            skSolve(sketch);
        }
        {
            var Q0;
            Q0=makeQuery(id+"F32.imprint","IMPRINT",FACE,{"disambiguationData":[TD([[makeQuery(id+"F32.imprint","IMPRINT",EDGE,{"derivedFrom":sQuery(id+"F32.wireOp",EDGE,"E42.bottom")}),1.0]])]});
            extrude(context, id + "F33", {"entities" : qUnion([Q0]), "operationType" : NewBodyOperationType.REMOVE, "endBound" : BoundingType.THROUGH_ALL, "depth" : 25 * mm, "offsetDistance" : 25 * mm});
        }
        {
            var Q0;
            {var subQ0=sQuery(id+"F19.wireOp",EDGE,"E27");var subQ1=sQuery(id+"F19.wireOp",EDGE,"E25");var subQ2=sQuery(id+"F3.wireOp",EDGE,"E4.left");var subQ3=sQuery(id+"F3.wireOp",EDGE,"E4.top");Q0=makeQuery(id+"F20.boolean.opBoolean","INTERSECT",VERTEX,{"derivedFrom":[makeQuery(id+"F7.opLoft","SWEPT_FACE",FACE,{"disambiguationData":[OSD([sQuery(id+"F3.wireOp",EDGE,"E4.bottom"),subQ3,subQ2,sQuery(id+"F6.wireOp",EDGE,"E6.bottom"),sQuery(id+"F6.wireOp",EDGE,"E6.top"),sQuery(id+"F6.wireOp",EDGE,"E6.left")])]}),makeQuery(id+"F8.opFillet","BLEND_FACE",FACE,{"disambiguationData":[OSD([subQ3,subQ2,sQuery(id+"F3.wireOp",EDGE,"E4.right")])]}),makeQuery(id+"F20.opExtrude","SWEPT_FACE",FACE,{"disambiguationData":[OSD([subQ0]),TDD([makeQuery(id+"F19.imprint","IMPRINT",EDGE,{"disambiguationData":[TD([[makeQuery(id+"F19.imprint","INTERSECT",VERTEX,{"disambiguationData":[OD(1.0)],"derivedFrom":[subQ1,subQ0]}),1.0]])],"derivedFrom":subQ0})])]})]});}
            var Q1;
            {var subQ0=sQuery(id+"F3.wireOp",EDGE,"E4.right");var subQ1=sQuery(id+"F3.wireOp",EDGE,"E4.left");var subQ2=sQuery(id+"F3.wireOp",EDGE,"E4.top");var subQ3=makeQuery(id+"F8.opFillet","BLEND_FACE",FACE,{"disambiguationData":[OSD([subQ2,subQ1,subQ0])]});var subQ4=sQuery(id+"F6.wireOp",EDGE,"E6.right");var subQ5=sQuery(id+"F6.wireOp",EDGE,"E6.left");var subQ6=sQuery(id+"F6.wireOp",EDGE,"E6.bottom");var subQ7=makeQuery(id+"F7.opLoft","SWEPT_FACE",FACE,{"disambiguationData":[OSD([subQ2,subQ1,subQ0,subQ6,subQ5,subQ4])]});var subQ8=sQuery(id+"F6.wireOp",EDGE,"E6.top");var subQ9=sQuery(id+"F3.wireOp",EDGE,"E4.bottom");var subQ10=makeQuery(id+"F7.opLoft","SWEPT_FACE",FACE,{"disambiguationData":[OSD([subQ9,subQ2,subQ1,subQ6,subQ8,subQ5])]});var subQ11=makeQuery(id+"F7.boolean.opBoolean","MERGE",EDGE,{"derivedFrom":[makeQuery(id+"F4.opLoft","MID_CAP_EDGE",EDGE,{"disambiguationData":[OSD([subQ2,subQ1,subQ0])],"capPos":1.0}),makeQuery(id+"F7.opLoft","MID_CAP_EDGE",EDGE,{"disambiguationData":[OSD([subQ2,subQ1,subQ0])],"capPos":0.0})]});var subQ12=makeQuery(id+"F21.opExtrude","SWEPT_EDGE",EDGE,{"disambiguationData":[OSD([subQ9,subQ2,subQ1,subQ0,subQ6,subQ8,subQ5,subQ4]),TDD([makeQuery(id+"F8.opFillet","BLEND_VERTEX",VERTEX,{"blendedFrom":[subQ11,subQ10,subQ7],"blendedInto":[subQ10,subQ7]})])]});var subQ14=makeQuery(id+"F22.opExtrude","CAP_EDGE",EDGE,{"disambiguationData":[OSD([subQ9,subQ2,subQ1,subQ0,subQ6,subQ8,subQ5,subQ4]),TDD([subQ12])],"isStart":false});Q1=makeQuery(id+"F30.opExtrude","CAP_VERTEX",VERTEX,{"disambiguationData":[OSD([subQ9,subQ2,subQ1,subQ0,subQ6,subQ8,subQ5,subQ4]),TDD([makeQuery(id+"F29.boolean.opBoolean","COPY",EDGE,{"derivedFrom":makeQuery(id+"F29.opExtrude","CAP_EDGE",EDGE,{"disambiguationData":[OSD([subQ9,subQ2,subQ1,subQ0,subQ6,subQ8,subQ5,subQ4]),TDD([makeQuery(id+"F22.boolean.opBoolean","MERGE",EDGE,{"derivedFrom":[subQ12,makeQuery(id+"F22.opExtrude","CAP_EDGE",EDGE,{"disambiguationData":[OSD([subQ9,subQ2,subQ1,subQ0,subQ6,subQ8,subQ5,subQ4]),TDD([subQ12])],"isStart":true})]})])],"isStart":false})}),makeQuery(id+"F29.boolean.opBoolean","COPY",EDGE,{"derivedFrom":makeQuery(id+"F29.opExtrude","CAP_EDGE",EDGE,{"disambiguationData":[OSD([subQ9,subQ2,subQ1,subQ0,subQ6,subQ8,subQ5,subQ4]),TDD([makeQuery(id+"F22.boolean.opBoolean","SPLIT",EDGE,{"disambiguationData":[topologyDisambiguationEdgeConnected([makeQuery(id+"F22.opExtrude","CAP_FACE",FACE,{"disambiguationData":[OSD([subQ2,subQ1,subQ0,subQ6,subQ5,subQ4]),TDD([makeQuery(id+"F21.opExtrude","SWEPT_FACE",FACE,{"disambiguationData":[OSD([subQ2,subQ1,subQ0,subQ6,subQ5,subQ4]),TDD([makeQuery(id+"F11.boolean.opBoolean","SPLIT",EDGE,{"disambiguationData":[TD([subQ10])],"derivedFrom":makeQuery(id+"F8.opFillet","BLEND_EDGE",EDGE,{"blendedFrom":[subQ11,subQ7],"blendedInto":[subQ7]})})])]})])],"isStart":false})])],"derivedFrom":subQ14}),makeQuery(id+"F22.boolean.opBoolean","SPLIT",EDGE,{"disambiguationData":[topologyDisambiguationEdgeConnected([subQ3])],"derivedFrom":subQ14})])],"isStart":false})})])],"isStart":false});}
            var Q2;
            {var subQ0=sQuery(id+"F6.wireOp",EDGE,"E6.right");var subQ1=sQuery(id+"F6.wireOp",EDGE,"E6.left");var subQ2=sQuery(id+"F6.wireOp",EDGE,"E6.bottom");var subQ3=sQuery(id+"F3.wireOp",EDGE,"E4.right");var subQ4=sQuery(id+"F3.wireOp",EDGE,"E4.left");var subQ5=sQuery(id+"F3.wireOp",EDGE,"E4.top");var subQ6=sQuery(id+"F6.wireOp",EDGE,"E6.top");var subQ7=sQuery(id+"F3.wireOp",EDGE,"E4.bottom");var subQ8=makeQuery(id+"F8.opFillet","BLEND_VERTEX",VERTEX,{"blendedFrom":[makeQuery(id+"F7.boolean.opBoolean","MERGE",EDGE,{"derivedFrom":[makeQuery(id+"F4.opLoft","MID_CAP_EDGE",EDGE,{"disambiguationData":[OSD([subQ5,subQ4,subQ3])],"capPos":1.0}),makeQuery(id+"F7.opLoft","MID_CAP_EDGE",EDGE,{"disambiguationData":[OSD([subQ5,subQ4,subQ3])],"capPos":0.0})]}),makeQuery(id+"F7.opLoft","SWEPT_FACE",FACE,{"disambiguationData":[OSD([subQ7,subQ5,subQ4,subQ2,subQ6,subQ1])]}),makeQuery(id+"F7.opLoft","SWEPT_FACE",FACE,{"disambiguationData":[OSD([subQ5,subQ4,subQ3,subQ2,subQ1,subQ0])]})],"blendedInto":[makeQuery(id+"F7.opLoft","SWEPT_FACE",FACE,{"disambiguationData":[OSD([subQ7,subQ5,subQ4,subQ2,subQ6,subQ1])]}),makeQuery(id+"F7.opLoft","SWEPT_FACE",FACE,{"disambiguationData":[OSD([subQ5,subQ4,subQ3,subQ2,subQ1,subQ0])]})]});var subQ9=makeQuery(id+"F22.boolean.opBoolean","MERGE",VERTEX,{"derivedFrom":[makeQuery(id+"F21.boolean.opBoolean","MERGE",VERTEX,{"derivedFrom":[subQ8,makeQuery(id+"F21.opExtrude","CAP_VERTEX",VERTEX,{"disambiguationData":[OSD([subQ7,subQ5,subQ4,subQ3,subQ2,subQ6,subQ1,subQ0]),TDD([subQ8])],"isStart":true})]}),makeQuery(id+"F22.opExtrude","CAP_VERTEX",VERTEX,{"disambiguationData":[OSD([subQ7,subQ5,subQ4,subQ3,subQ2,subQ6,subQ1,subQ0]),TDD([makeQuery(id+"F21.opExtrude","SWEPT_EDGE",EDGE,{"disambiguationData":[OSD([subQ7,subQ5,subQ4,subQ3,subQ2,subQ6,subQ1,subQ0]),TDD([subQ8])]})])],"isStart":false})]});Q2=makeQuery(id+"F29.boolean.opBoolean","MERGE",VERTEX,{"derivedFrom":[subQ9],"fromTools":[makeQuery(id+"F29.opExtrude","CAP_VERTEX",VERTEX,{"disambiguationData":[OSD([subQ7,subQ5,subQ4,subQ3,subQ2,subQ6,subQ1,subQ0]),TDD([subQ9])],"isStart":true})]});}
            cPlane(context, id + "F34", {"entities" : qUnion([Q0, Q1, Q2]), "cplaneType" : CPlaneType.THREE_POINT, "offset" : 25 * mm, "width" : 150 * mm, "height" : 150 * mm});
        }
        {
            var Q0;
            Q0=qCreatedBy(id+"F34.planeOp",FACE);
            var sketch = newSketch(context, id + "F35", { "sketchPlane" : qUnion([Q0])});
            skEllipticalArc(sketch, "E46.0.0", {});
            skLineSegment(sketch, "E46.0.1", {"start": v(-13.64, 4.19) * mm, "end": v(-13.9, 4.19) * mm});
            skFitSpline(sketch, "E46.0.2", {"points": [v(-13.9, 4.86) * mm, v(-13.9, 4.53) * mm, v(-13.88, 4.2) * mm, v(-13.86, 3.88) * mm]});
            const initialGuessF35  = {"E46.0.0": [-0.01371774963059614, 0.004367151228198279, -0.1413885674954577, -0.9899541772130579, 0.005050729022227157, 6.96813033104161e-05, 4.616090899644146, 4.812627919537867]};
            skSetInitialGuess(sketch, initialGuessF35);
            skSolve(sketch);
        }
        {
            var Q0;
            Q0 = qSketchRegion(id + "F35", true);
            extrude(context, id + "F36", {"entities" : qUnion([Q0]), "operationType" : NewBodyOperationType.REMOVE, "endBound" : BoundingType.THROUGH_ALL, "oppositeDirection" : true, "depth" : 25 * mm, "offsetDistance" : 25 * mm, "hasSecondDirection" : true, "secondDirectionOppositeDirection" : false, "secondDirectionDepth" : 0.2 * mm});
        }
    });
